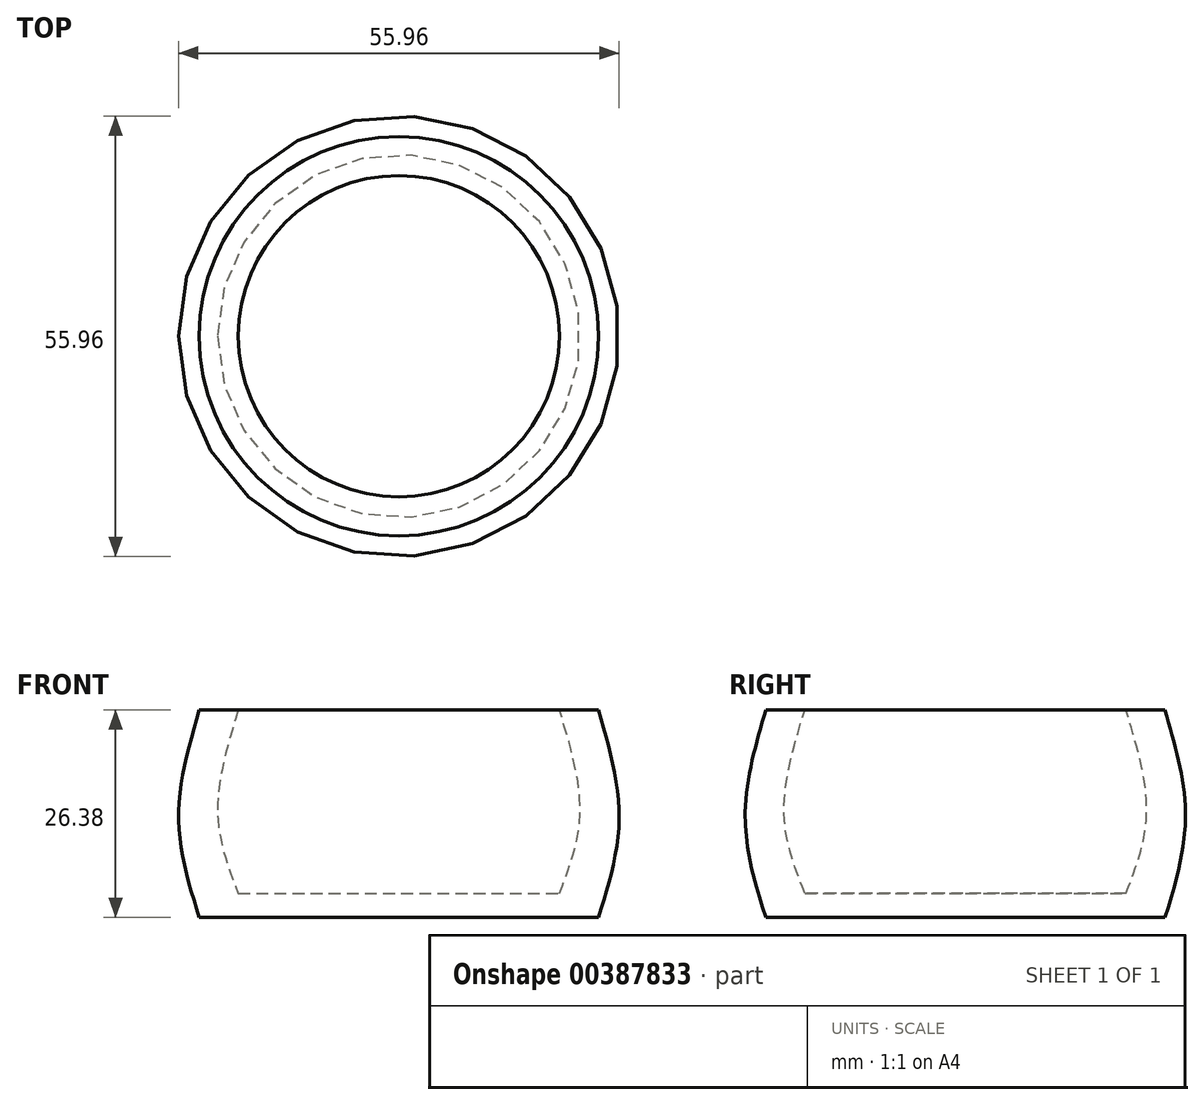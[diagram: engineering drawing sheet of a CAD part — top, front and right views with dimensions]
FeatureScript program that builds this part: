
annotation { "Feature Type Name" : "Feature", "Feature Type Description" : "" }
export const myFeature = defineFeature(function(context is Context, id is Id, definition is map)
    precondition{}
    {
        {
            var Q0;
            Q0=qCreatedBy(makeId("Front.planeOp"),FACE);
            var sketch = newSketch(context, id + "F0", { "sketchPlane" : qUnion([Q0])});
            skLineSegment(sketch, "E0", {"start": v(0, 0) * mm, "end": v(25.36, 0) * mm});
            skFitSpline(sketch, "E1", {"points": [v(25.36, 0) * mm, v(27.98, 12.68) * mm, v(25.36, 26.38) * mm], "startDerivative": vector(7.92, 25.58) * mm, "endDerivative": vector(-7.82, 27.17) * mm});
            skLineSegment(sketch, "E2", {"start": v(25.36, 26.38) * mm, "end": v(20.4, 26.38) * mm});
            skFitSpline(sketch, "E3", {"points": [v(20.4, 26.38) * mm, v(23.03, 13.26) * mm, v(20.4, 3.06) * mm], "startDerivative": vector(7.74, -25.57) * mm, "endDerivative": vector(-8.05, -20.98) * mm});
            skLineSegment(sketch, "E4", {"start": v(20.4, 3.06) * mm, "end": v(0, 3.06) * mm});
            skLineSegment(sketch, "E5", {"start": v(0, 3.06) * mm, "end": v(0, 0) * mm});
            skLineSegment(sketch, "E6", {"start": v(0, 0) * mm, "end": v(0, 27.84) * mm, "construction": true});
            skSolve(sketch);
        }
        {
            var Q0;
            Q0=makeQuery(id+"F0.imprint","IMPRINT",FACE,{"disambiguationData":[TD([[makeQuery(id+"F0.imprint","IMPRINT",EDGE,{"derivedFrom":sQuery(id+"F0.wireOp",EDGE,"E0")}),1.0]])]});
            var Q1;
            Q1=sQuery(id+"F0.wireOp",EDGE,"E6");
            revolve(context, id + "F1", {"entities" : qUnion([Q0]), "axis" : qUnion([Q1]), "revolveType" : RevolveType.FULL});
        }
    });
